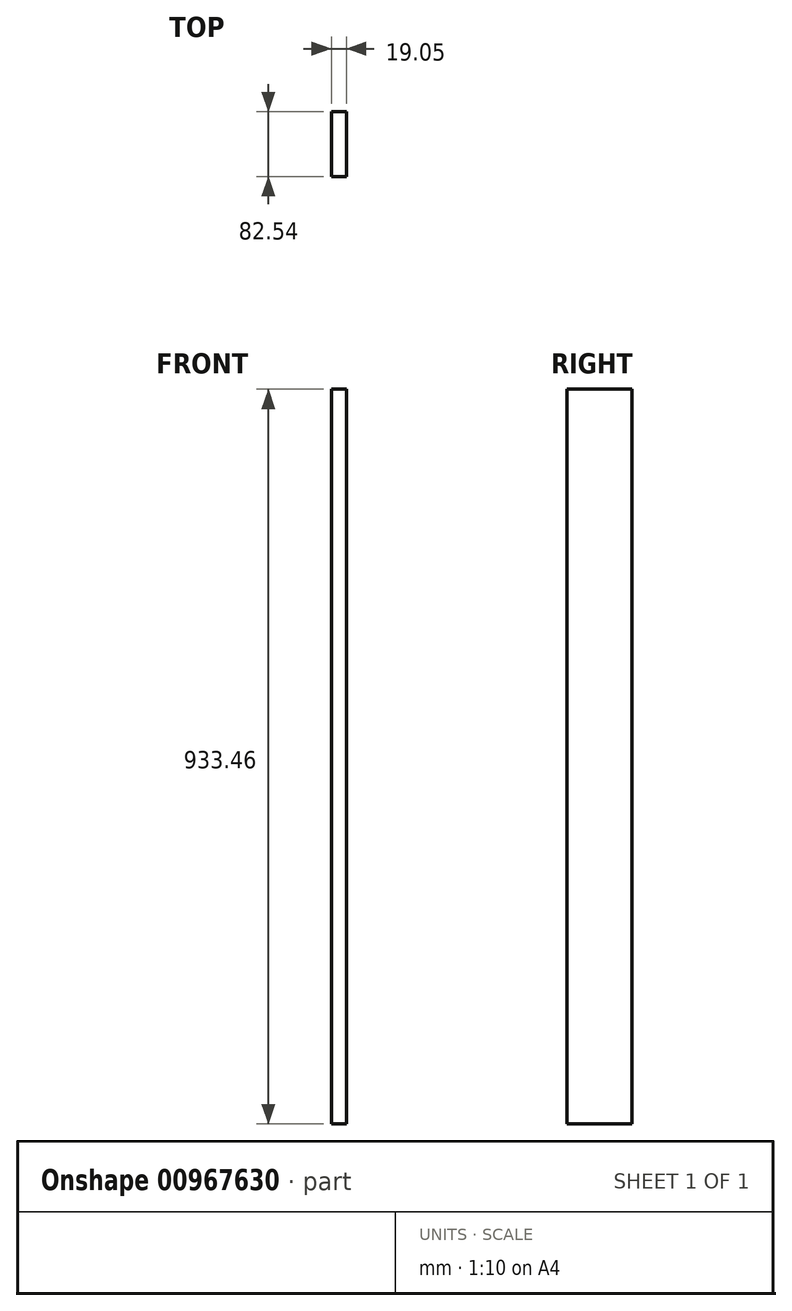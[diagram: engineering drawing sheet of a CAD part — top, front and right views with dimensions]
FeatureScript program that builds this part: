
annotation { "Feature Type Name" : "Feature", "Feature Type Description" : "" }
export const myFeature = defineFeature(function(context is Context, id is Id, definition is map)
    precondition{}
    {
        {
            var Q0;
            Q0=qCreatedBy(makeId("Right.planeOp"),FACE);
            var sketch = newSketch(context, id + "F0", { "sketchPlane" : qUnion([Q0])});
            skLineSegment(sketch, "E0.bottom", {"start": v(41.27, 466.73) * mm, "end": v(-41.28, 466.73) * mm});
            skLineSegment(sketch, "E0.top", {"start": v(41.28, -466.73) * mm, "end": v(-41.27, -466.73) * mm});
            skLineSegment(sketch, "E0.left", {"start": v(41.27, 466.73) * mm, "end": v(41.28, -466.73) * mm});
            skLineSegment(sketch, "E0.right", {"start": v(-41.28, 466.73) * mm, "end": v(-41.27, -466.73) * mm});
            skPoint(sketch, "E0.middle", {"position": v(0, 0) * mm});
            skSolve(sketch);
        }
        {
            var Q0;
            Q0 = qSketchRegion(id + "F0", true);
            extrude(context, id + "F1", {"entities" : qUnion([Q0]), "depth" : 19.05 * mm, "offsetDistance" : 25.4 * mm});
        }
    });
